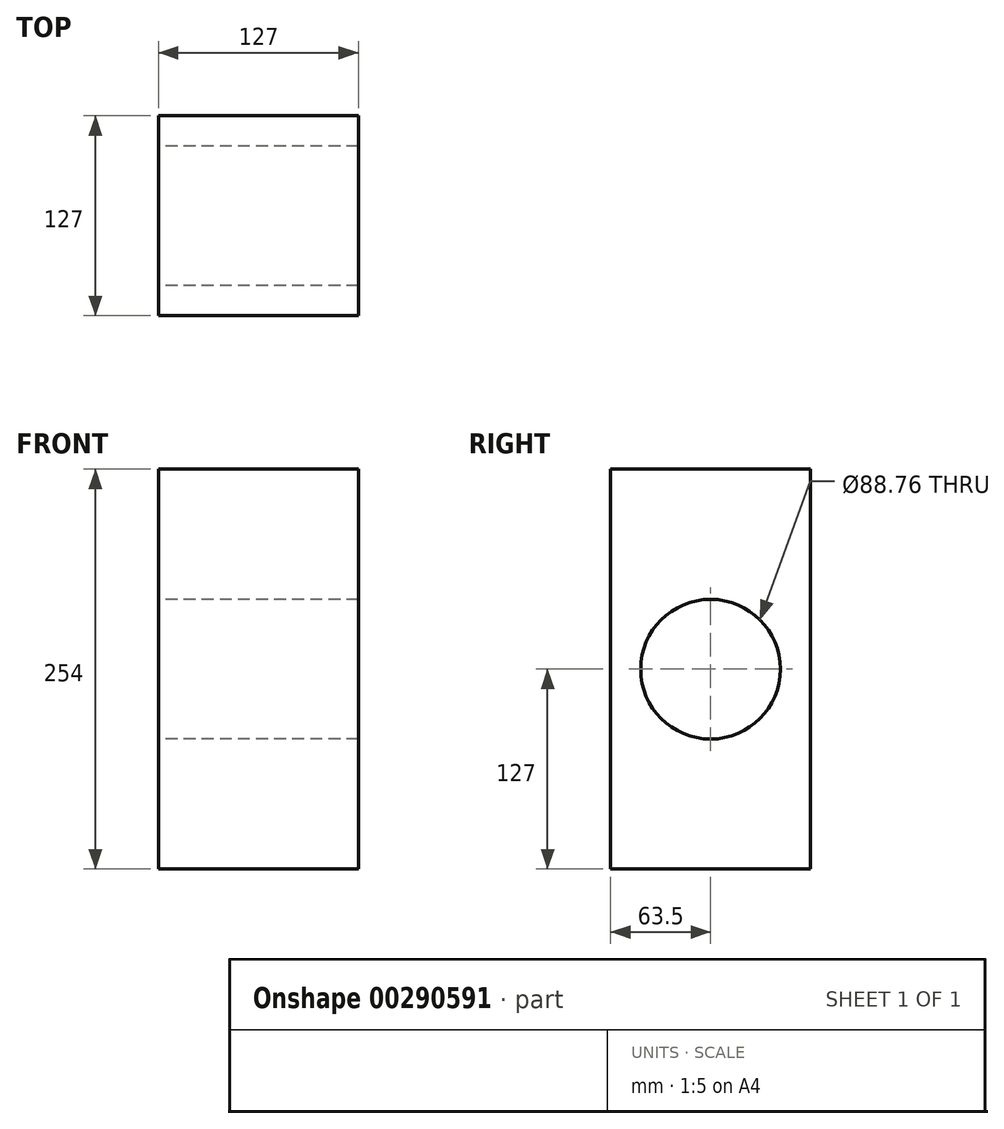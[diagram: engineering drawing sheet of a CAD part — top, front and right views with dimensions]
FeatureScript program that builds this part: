
annotation { "Feature Type Name" : "Feature", "Feature Type Description" : "" }
export const myFeature = defineFeature(function(context is Context, id is Id, definition is map)
    precondition{}
    {
        {
            var Q0;
            Q0=qCreatedBy(makeId("Front.planeOp"),FACE);
            var sketch = newSketch(context, id + "F0", { "sketchPlane" : qUnion([Q0])});
            skLineSegment(sketch, "E0.bottom", {"start": v(0, 0) * mm, "end": v(127, 0) * mm});
            skLineSegment(sketch, "E0.top", {"start": v(0, 254) * mm, "end": v(127, 254) * mm});
            skLineSegment(sketch, "E0.left", {"start": v(0, 0) * mm, "end": v(0, 254) * mm});
            skLineSegment(sketch, "E0.right", {"start": v(127, 0) * mm, "end": v(127, 254) * mm});
            skSolve(sketch);
        }
        {
            var Q0;
            Q0=makeQuery(id+"F0.imprint","IMPRINT",FACE,{"disambiguationData":[TD([[makeQuery(id+"F0.imprint","IMPRINT",EDGE,{"derivedFrom":sQuery(id+"F0.wireOp",EDGE,"E0.bottom")}),1.0]])]});
            extrude(context, id + "F1", {"entities" : qUnion([Q0]), "depth" : 127 * mm});
        }
        {
            var Q0;
            Q0=makeQuery(id+"F1.opExtrude","SWEPT_FACE",FACE,{"disambiguationData":[OSD([sQuery(id+"F0.wireOp",EDGE,"E0.left")])]});
            var sketch = newSketch(context, id + "F2", { "sketchPlane" : qUnion([Q0])});
            skCircle(sketch, "E1", {"center": v(63.5, 127) * mm, "radius": 44.38 * mm});
            skSolve(sketch);
        }
        {
            var Q0;
            Q0 = qSketchRegion(id + "F2", true);
            var Q1;
            Q1=makeQuery(id+"F1.opExtrude","SWEPT_FACE",FACE,{"disambiguationData":[OSD([sQuery(id+"F0.wireOp",EDGE,"E0.right")])]});
            extrude(context, id + "F3", {"entities" : qUnion([Q0]), "operationType" : NewBodyOperationType.REMOVE, "endBound" : BoundingType.UP_TO_SURFACE, "oppositeDirection" : true, "endBoundEntityFace" : qUnion([Q1]), "depth" : 25.4 * mm});
        }
    });
